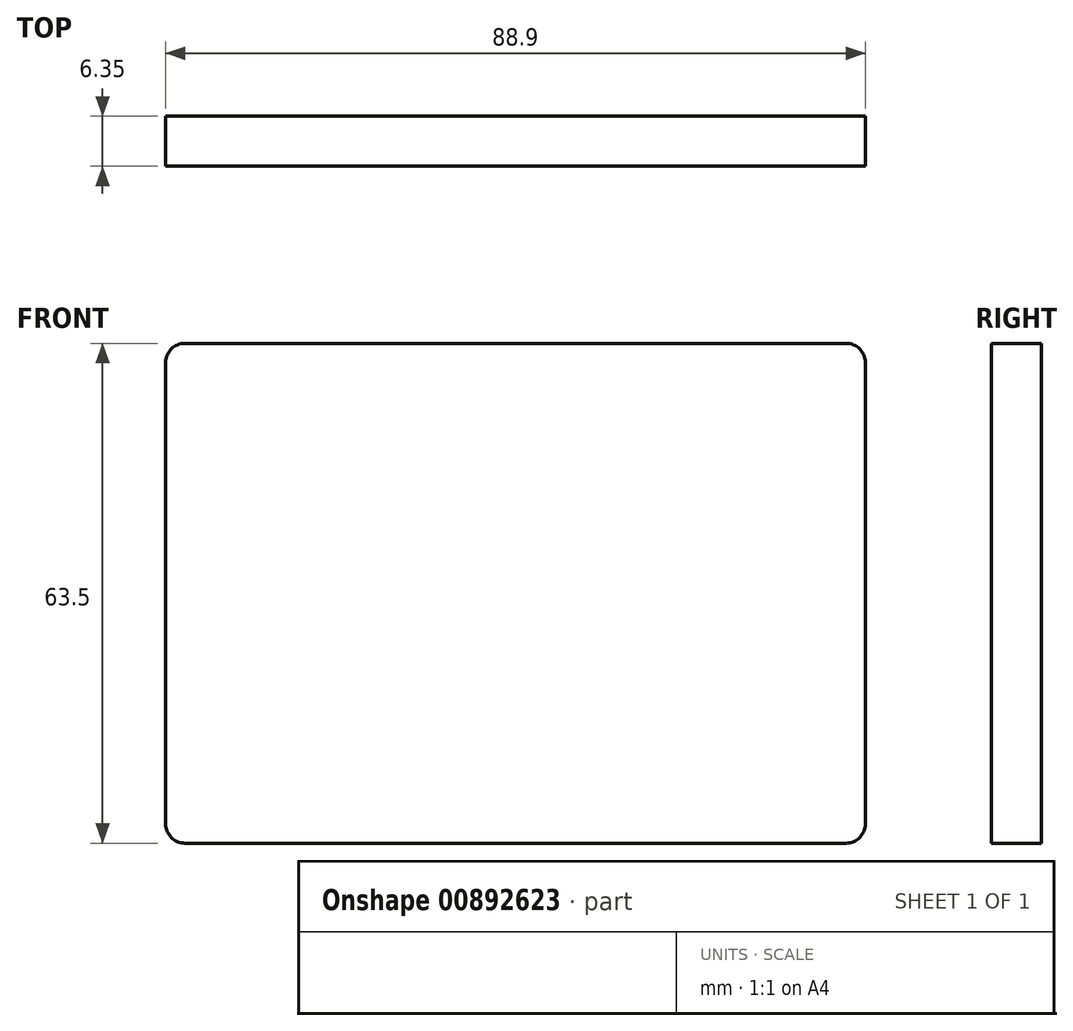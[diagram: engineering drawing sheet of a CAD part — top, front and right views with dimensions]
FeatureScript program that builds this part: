
annotation { "Feature Type Name" : "Feature", "Feature Type Description" : "" }
export const myFeature = defineFeature(function(context is Context, id is Id, definition is map)
    precondition{}
    {
        {
            var Q0;
            Q0=qCreatedBy(makeId("Front.planeOp"),FACE);
            var sketch = newSketch(context, id + "F0", { "sketchPlane" : qUnion([Q0])});
            skLineSegment(sketch, "E0.bottom", {"start": v(-42.77, 37.2) * mm, "end": v(46.13, 37.2) * mm});
            skLineSegment(sketch, "E0.top", {"start": v(-42.77, -26.3) * mm, "end": v(46.13, -26.3) * mm});
            skLineSegment(sketch, "E0.left", {"start": v(-42.77, 37.2) * mm, "end": v(-42.77, -26.3) * mm});
            skLineSegment(sketch, "E0.right", {"start": v(46.13, 37.2) * mm, "end": v(46.13, -26.3) * mm});
            skSolve(sketch);
        }
        {
            var Q0;
            Q0=makeQuery(id+"F0.imprint","IMPRINT",FACE,{"disambiguationData":[TD([[makeQuery(id+"F0.imprint","IMPRINT",EDGE,{"derivedFrom":sQuery(id+"F0.wireOp",EDGE,"E0.bottom")}),-1.0]])]});
            extrude(context, id + "F1", {"entities" : qUnion([Q0]), "depth" : 6.35 * mm, "offsetDistance" : 25.4 * mm});
        }
        {
            var Q0;
            Q0=makeQuery(id+"F1.opExtrude","SWEPT_EDGE",EDGE,{"disambiguationData":[OSD([sQuery(id+"F0.wireOp",EDGE,"E0.bottom"),sQuery(id+"F0.wireOp",EDGE,"E0.left")])]});
            fillet(context, id + "F2", {"entities" : qUnion([Q0]), "radius" : 2.45 * mm, "tangentPropagation" : true, "allowEdgeOverflow" : false});
        }
        {
            var Q0;
            Q0=makeQuery(id+"F1.opExtrude","SWEPT_EDGE",EDGE,{"disambiguationData":[OSD([sQuery(id+"F0.wireOp",EDGE,"E0.bottom"),sQuery(id+"F0.wireOp",EDGE,"E0.right")])]});
            var Q1;
            Q1=makeQuery(id+"F1.opExtrude","SWEPT_EDGE",EDGE,{"disambiguationData":[OSD([sQuery(id+"F0.wireOp",EDGE,"E0.top"),sQuery(id+"F0.wireOp",EDGE,"E0.left")])]});
            var Q2;
            Q2=makeQuery(id+"F1.opExtrude","SWEPT_EDGE",EDGE,{"disambiguationData":[OSD([sQuery(id+"F0.wireOp",EDGE,"E0.top"),sQuery(id+"F0.wireOp",EDGE,"E0.right")])]});
            fillet(context, id + "F3", {"entities" : qUnion([Q0, Q1, Q2]), "radius" : 2.46 * mm, "tangentPropagation" : true, "allowEdgeOverflow" : false});
        }
    });
